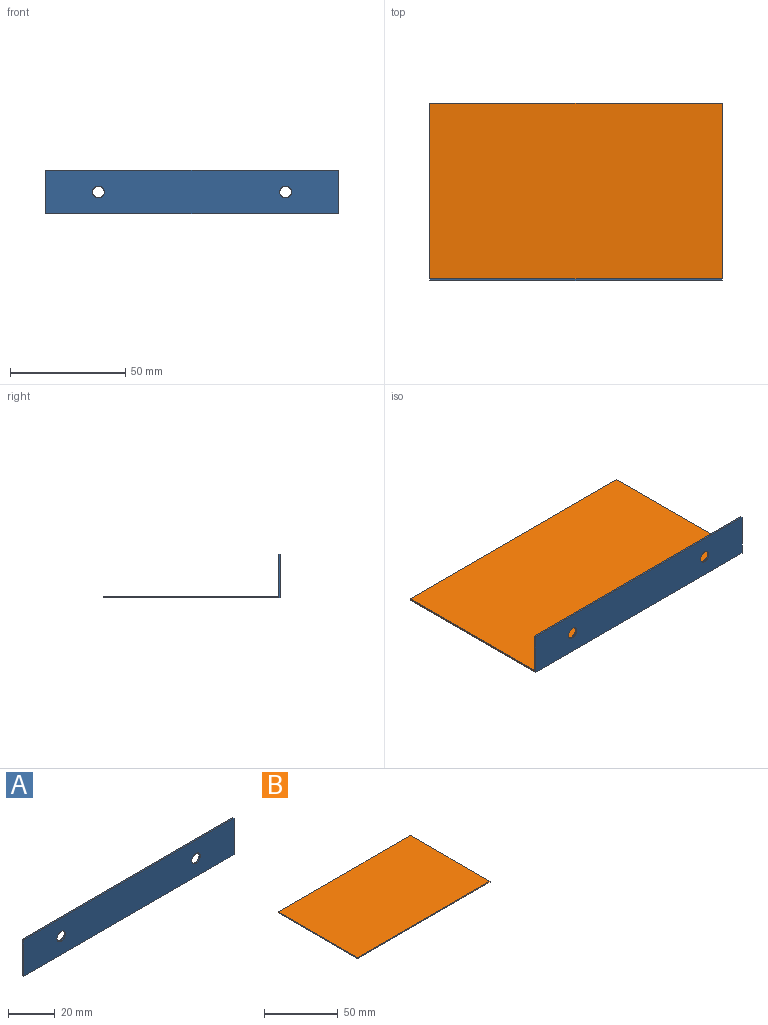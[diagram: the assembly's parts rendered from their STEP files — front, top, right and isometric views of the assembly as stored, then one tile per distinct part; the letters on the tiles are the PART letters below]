
ASSEMBLY  parts=2 mates=1
PART A: 8 faces, bbox 127x0.8x19.1 mm
  f0: plane 19.05x0.76mm, normal (1,0,0), area 14.5mm2, adj f1,f3,f4,f5
  f1: plane 127x0.76mm, normal (0,0,1), area 96.8mm2, adj f0,f2,f4,f5
  f2: plane 19.05x0.76mm, normal (-1,0,0), area 14.5mm2, adj f1,f3,f4,f5
  f3: plane 127x0.76mm, normal (0,0,-1), area 96.8mm2, adj f0,f2,f4,f5
  f4: plane 127x19.05mm, normal (0,-1,0), area 2378.4mm2, adj f0,f1,f2,f3,f6,f7
  f5: plane 127x19.05mm, normal (0,1,0), area 2378.4mm2, adj f0,f1,f2,f3,f6,f7
  f6: cylinder r=2.55mm len=5.11mm, axis (0,1,0), area 12.2mm2, adj f4,f5
  f7: cylinder r=2.55mm len=5.11mm, axis (0,1,0), area 12.2mm2, adj f4,f5
PART B: 6 faces, bbox 127x76.2x0.8 mm
  f0: plane 127x0.76mm, normal (0,1,0), area 96.8mm2, adj f1,f3,f4,f5
  f1: plane 76.2x0.76mm, normal (-1,0,0), area 58.1mm2, adj f0,f2,f4,f5
  f2: plane 127x0.76mm, normal (0,-1,0), area 96.8mm2, adj f1,f3,f4,f5
  f3: plane 76.2x0.76mm, normal (1,0,0), area 58.1mm2, adj f0,f2,f4,f5
  f4: plane 127x76.2mm, normal (0,0,1), area 9677.4mm2, adj f0,f1,f2,f3
  f5: plane 127x76.2mm, normal (0,0,-1), area 9677.4mm2, adj f0,f1,f2,f3
PLACE A t=(-40.58,-60.71,10.38)mm
PLACE B t=(-40.58,-22.61,0.85)mm
MATE fastened A.f5 <-> B.f2  axis (0,1,0) through (22.92,-60.71,0.85)mm
